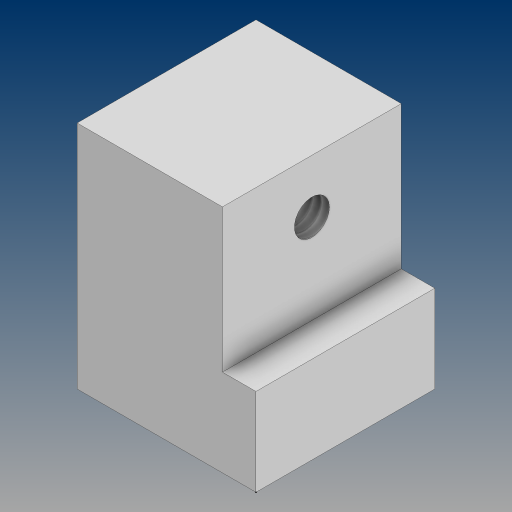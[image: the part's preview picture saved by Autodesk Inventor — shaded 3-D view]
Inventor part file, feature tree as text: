
AUTODESK INVENTOR PART (.ipt)
format: ipt  version: 2024.3 (Build 283343000, 343)  size: 159,232 bytes
history: native  units: in
note: dims shown in document units (in); Inventor stores cm internally (conversion verified against a paired STEP export)
features: sketch x7, extrude x4, hole x3, projected_geometry x1
ambient origin geometry x8: Origin, YZ Plane, XZ Plane, XY Plane, X Axis, Y Axis, Z Axis, Center Point
bodies: Solid1 (feature_tree)
feature tree (15):
  extrude  "Extrusion1"  Depth=1.0in
  hole  "Hole1"  [1 undecoded]
  hole  "Hole2"  [1 undecoded]
  sketch  "Sketch4"  dims[d6=0.196in d7=0.5in d8=0.375in d9=0.25in d10=0.5635in d11=0.75in d12=0.0in d13=0.5in]
  extrude  "Extrusion2"  Depth=0.1875in
  extrude  "Extrusion3"  Depth=1.0in TaperAngle=0.0deg
  hole  "Hole3"  [1 undecoded]
  sketch  "Sketch7"  dims[d15=0.196in d16=0.5in d17=0.375in d18=0.25in d19=0.5635in d20=1.0in d21=0.0in d22=0.1875in]
  extrude  "Extrusion4"  Depth=1.0in
  sketch  "Sketch1"  dims[d0=1.0in d1=1.0in]
  sketch  "Sketch2"  dims[d2=1.488in d3=0.0in d4=0.5in]
  sketch  "Sketch3"  dims[d5=0.5in]
  projected_geometry  "Projected Loop1"
  sketch  "Sketch6"  dims[d14=0.5in]
  sketch  "Sketch8"  dims[d24=1.0in d25=0.0in d26=1.0in d27=0.0in d28=0.5in d29=0.5in d30=0.196in d31=1.0in d32=0.375in d33=0.25in d34=0.5635in d35=1.0in d36=0.0in d37=0.2in d38=0.0in d23=0.8108in d39=0.0625in d40=0.75in d41=0.375in]
note: 3 required parameter values undecoded (feature->parameter linkage not recoverable at this tier; creation-order binding heuristic only, values carry confidence <= 0.55)
